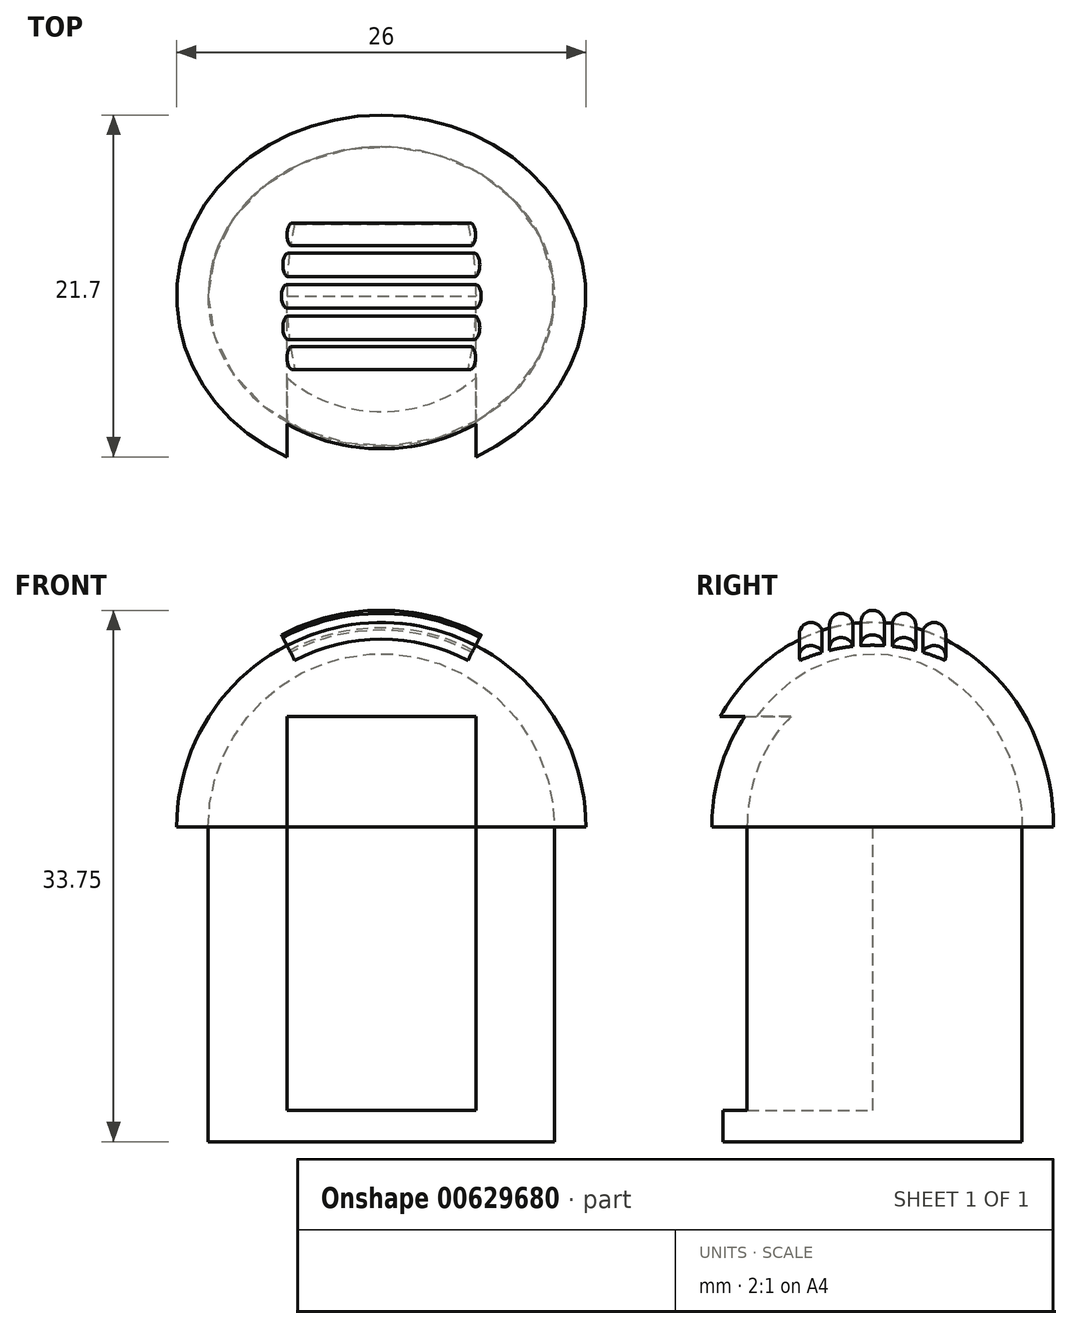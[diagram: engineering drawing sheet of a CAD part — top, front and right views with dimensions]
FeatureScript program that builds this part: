
annotation { "Feature Type Name" : "Feature", "Feature Type Description" : "" }
export const myFeature = defineFeature(function(context is Context, id is Id, definition is map)
    precondition{}
    {
        {
            var Q0;
            Q0=qCreatedBy(makeId("Top.planeOp"),FACE);
            var sketch = newSketch(context, id + "F0", { "sketchPlane" : qUnion([Q0])});
            skEllipse(sketch, "E0", {"center": v(0, 0) * mm, "majorRadius": 11 * mm, "minorRadius": 9.5 * mm, "majorAxis": v(-1, 0)});
            skFitSpline(sketch, "E1.0", {"points": [v(-12.96, 1.16) * mm, v(-13.02, 0) * mm, v(-12.96, -1.16) * mm, v(-12.7, -2.7) * mm, v(-12.18, -4.16) * mm, v(-11.42, -5.54) * mm, v(-10.52, -6.84) * mm, v(-9.14, -8.29) * mm, v(-7.5, -9.46) * mm, v(-6.03, -10.21) * mm, v(-4.5, -10.83) * mm, v(-2.9, -11.25) * mm, v(-1.25, -11.46) * mm, v(0, -11.52) * mm, v(1.25, -11.46) * mm, v(2.9, -11.25) * mm, v(4.5, -10.83) * mm, v(6.03, -10.21) * mm, v(7.5, -9.46) * mm, v(9.14, -8.29) * mm, v(10.52, -6.84) * mm, v(11.42, -5.54) * mm, v(12.18, -4.16) * mm, v(12.7, -2.7) * mm, v(12.96, -1.16) * mm, v(13.02, 0) * mm, v(12.96, 1.16) * mm, v(12.7, 2.7) * mm, v(12.18, 4.16) * mm, v(11.42, 5.54) * mm, v(10.52, 6.84) * mm, v(9.14, 8.29) * mm, v(7.5, 9.46) * mm, v(6.03, 10.21) * mm, v(4.5, 10.83) * mm, v(2.9, 11.25) * mm, v(1.25, 11.46) * mm, v(0, 11.52) * mm, v(-1.25, 11.46) * mm, v(-2.9, 11.25) * mm, v(-4.5, 10.83) * mm, v(-6.03, 10.21) * mm, v(-7.5, 9.46) * mm, v(-9.14, 8.29) * mm, v(-10.52, 6.84) * mm, v(-11.42, 5.54) * mm, v(-12.18, 4.16) * mm, v(-12.7, 2.7) * mm, v(-12.96, 1.16) * mm, v(-13.02, 0) * mm, v(-12.96, -1.16) * mm, v(-12.96, 1.16) * mm]});
            skSolve(sketch);
        }
        {
            var Q0;
            Q0=qSketchRegion(id+"F0",true);
            extrude(context, id + "F1", {"entities" : qUnion([Q0]), "depth" : 20 * mm, "offsetDistance" : 25 * mm});
        }
        {
            var Q0;
            Q0=makeQuery(id+"F1.opExtrude","CAP_FACE",FACE,{"disambiguationData":[OSD([sQuery(id+"F0.wireOp",EDGE,"E0")])],"isStart":false});
            var sketch = newSketch(context, id + "F2", { "sketchPlane" : qUnion([Q0])});
            skLineSegment(sketch, "E2", {"start": v(0, -11.5) * mm, "end": v(0, 11.5) * mm, "construction": true});
            skLineSegment(sketch, "E3", {"start": v(-13, 0) * mm, "end": v(13, 0) * mm, "construction": true});
            skPoint(sketch, "E3.endSnap0", {"position": v(11, 0) * mm});
            skEllipticalArc(sketch, "E4", {});
            skLineSegment(sketch, "E5", {"start": v(0, 11.5) * mm, "end": v(0, 9.5) * mm});
            skLineSegment(sketch, "E6", {"start": v(0, -9.5) * mm, "end": v(0, -11.5) * mm});
            skEllipticalArc(sketch, "E7", {});
            const initialGuessF2  = {"E4": [0, 0, -1, 0, 0.013, 0.0115, 4.71238898038469, 3.141592653589793], "E7": [0, 0, -1, 0, 0.011, 0.0095, 4.71238898038469, 1.5707963267948966]};
            skSetInitialGuess(sketch, initialGuessF2);
            skSolve(sketch);
        }
        {
            var Q0;
            {var subQ4=sQuery(id+"F2.wireOp",EDGE,"E5");Q0=makeQuery(id+"F2.imprint","IMPRINT",FACE,{"disambiguationData":[TD([[makeQuery(id+"F2.imprint","IMPRINT",EDGE,{"derivedFrom":subQ4}),-1.0]])]});}
            var Q1;
            Q1=sQuery(id+"F2.wireOp",EDGE,"E2");
            revolve(context, id + "F3", {"entities" : qUnion([Q0]), "axis" : qUnion([Q1]), "revolveType" : RevolveType.ONE_DIRECTION, "angle" : 180 * degree});
        }
        {
            var Q0;
            Q0=qCreatedBy(makeId("Front.planeOp"),FACE);
            var sketch = newSketch(context, id + "F4", { "sketchPlane" : qUnion([Q0])});
            skPoint(sketch, "E8.center.orphan", {"position": v(0, 0) * mm});
            skLineSegment(sketch, "E9.bottom", {"start": v(-6, 27) * mm, "end": v(6, 27) * mm});
            skLineSegment(sketch, "E9.top", {"start": v(-6, 2) * mm, "end": v(6, 2) * mm});
            skLineSegment(sketch, "E9.left", {"start": v(-6, 27) * mm, "end": v(-6, 2) * mm});
            skLineSegment(sketch, "E9.right", {"start": v(6, 27) * mm, "end": v(6, 2) * mm});
            skSolve(sketch);
        }
        {
            var Q0;
            Q0=qSketchRegion(id+"F4",true);
            extrude(context, id + "F5", {"entities" : qUnion([Q0]), "operationType" : NewBodyOperationType.REMOVE, "endBound" : BoundingType.THROUGH_ALL, "depth" : 25 * mm, "offsetDistance" : 25 * mm});
        }
        {
            var Q0;
            Q0=qCreatedBy(makeId("Right.planeOp"),FACE);
            var sketch = newSketch(context, id + "F6", { "sketchPlane" : qUnion([Q0])});
            skLineSegment(sketch, "E10", {"start": v(0, 0) * mm, "end": v(0, 33) * mm, "construction": true});
            skLineSegment(sketch, "E11", {"start": v(-18.13, 20) * mm, "end": v(26.01, 20) * mm, "construction": true});
            skEllipticalArc(sketch, "E12", {});
            skArc(sketch, "E13", {"start": v(0.75, 32.97) * mm, "mid": v(0, 33.75) * mm, "end": v(-0.75, 32.97) * mm});
            skArc(sketch, "E14", {"start": v(-1.25, 32.92) * mm, "mid": v(-2.14, 33.54) * mm, "end": v(-2.72, 32.63) * mm});
            skArc(sketch, "E15", {"start": v(2.72, 32.63) * mm, "mid": v(2.14, 33.54) * mm, "end": v(1.25, 32.92) * mm});
            skArc(sketch, "E16", {"start": v(-3.2, 32.49) * mm, "mid": v(-4.19, 32.92) * mm, "end": v(-4.59, 31.92) * mm});
            skArc(sketch, "E17", {"start": v(4.59, 31.92) * mm, "mid": v(4.19, 32.92) * mm, "end": v(3.2, 32.49) * mm});
            const initialGuessF6  = {"E12": [0, 0.02, 1, 0, 0.0115, 0.013, 6.283185307179586, 3.141592653589793]};
            skSetInitialGuess(sketch, initialGuessF6);
            skSolve(sketch);
        }
        {
            var Q0;
            Q0=qCreatedBy(makeId("Front.planeOp"),FACE);
            var sketch = newSketch(context, id + "F7", { "sketchPlane" : qUnion([Q0])});
            skLineSegment(sketch, "E18", {"start": v(0, 53.6) * mm, "end": v(0, -9.03) * mm, "construction": true});
            skLineSegment(sketch, "E19", {"start": v(-27.45, 20) * mm, "end": v(-13, 20) * mm, "construction": true});
            skEllipticalArc(sketch, "E20", {});
            skLineSegment(sketch, "E21.trimOffspring", {"start": v(13, 20) * mm, "end": v(34.84, 20) * mm, "construction": true});
            skLineSegment(sketch, "E22", {"start": v(6, 20) * mm, "end": v(6, 31.53) * mm, "construction": true});
            skLineSegment(sketch, "E23", {"start": v(-6, 20) * mm, "end": v(-6, 31.53) * mm, "construction": true});
            const initialGuessF7  = {"E20": [0, 0.02, 1, 0, 0.013, 0.013, 1.0910676891191438, 2.050524964470649]};
            skSetInitialGuess(sketch, initialGuessF7);
            skSolve(sketch);
        }
        {
            var Q0;
            Q0 = qSketchRegion(id + "F6", true);
            var Q1;
            Q1=sQuery(id+"F7.wireOp",EDGE,"E20");
            sweep(context, id + "F8", {"profiles" : qUnion([Q0]), "path" : qUnion([Q1])});
        }
    });
